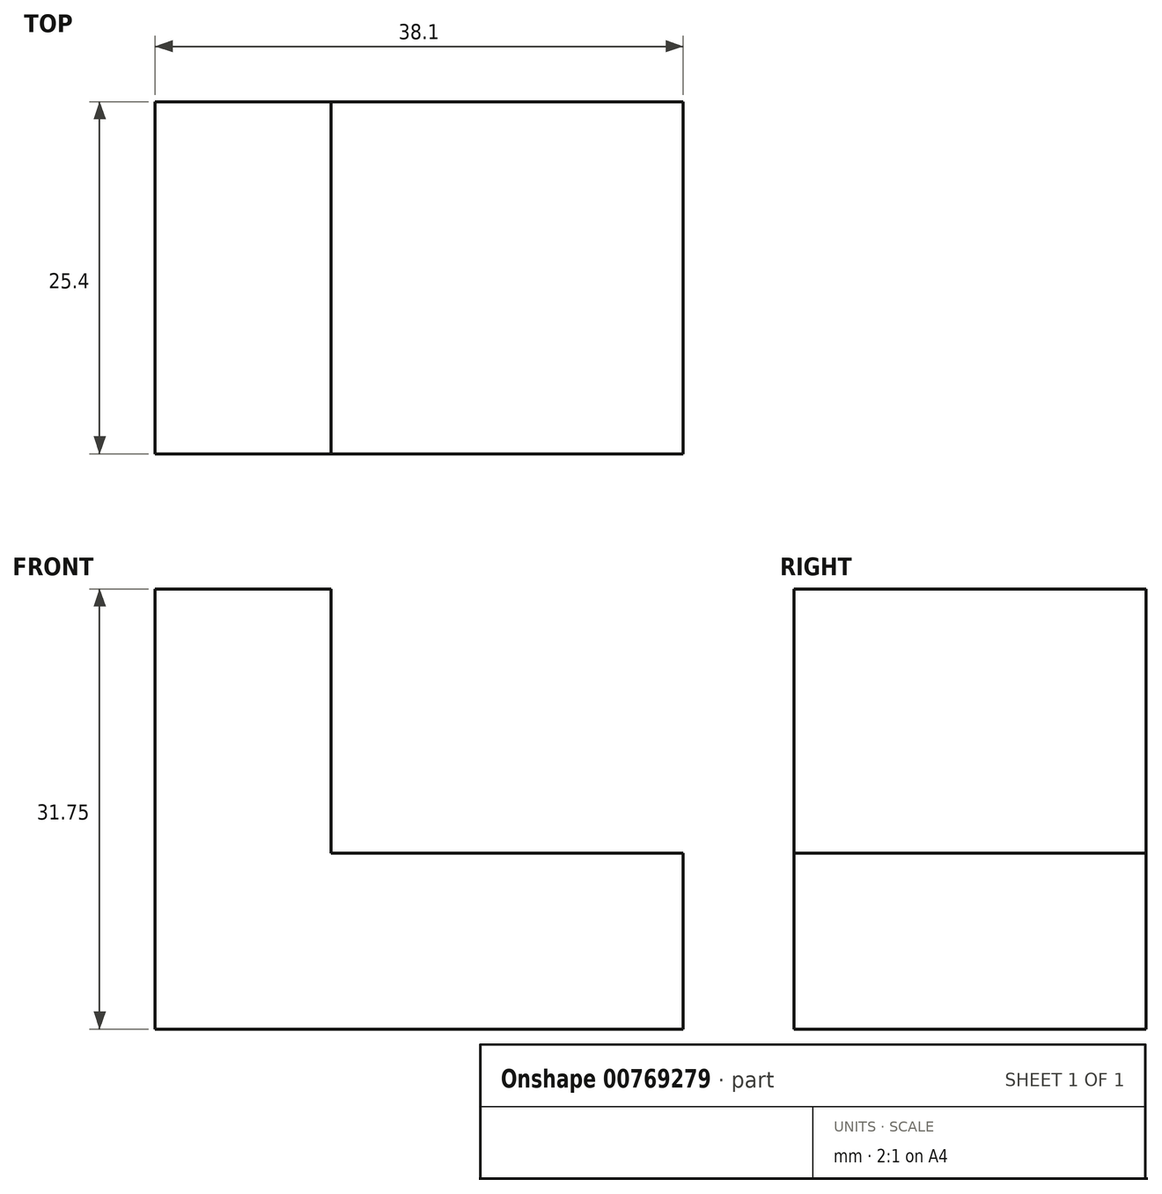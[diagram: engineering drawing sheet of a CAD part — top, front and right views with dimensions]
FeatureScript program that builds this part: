
annotation { "Feature Type Name" : "Feature", "Feature Type Description" : "" }
export const myFeature = defineFeature(function(context is Context, id is Id, definition is map)
    precondition{}
    {
        {
            var Q0;
            Q0=qCreatedBy(makeId("Front.planeOp"),FACE);
            var sketch = newSketch(context, id + "F0", { "sketchPlane" : qUnion([Q0])});
            skLineSegment(sketch, "E0", {"start": v(0, 0) * mm, "end": v(0, 31.75) * mm});
            skLineSegment(sketch, "E1", {"start": v(0, 31.75) * mm, "end": v(0, 0) * mm});
            skLineSegment(sketch, "E2", {"start": v(0, 31.75) * mm, "end": v(12.7, 31.75) * mm});
            skLineSegment(sketch, "E3", {"start": v(12.7, 31.75) * mm, "end": v(12.7, 12.7) * mm});
            skLineSegment(sketch, "E4", {"start": v(12.7, 12.7) * mm, "end": v(38.1, 12.7) * mm});
            skLineSegment(sketch, "E5", {"start": v(38.1, 12.7) * mm, "end": v(38.1, 0) * mm});
            skLineSegment(sketch, "E6", {"start": v(38.1, 0) * mm, "end": v(0, 0) * mm});
            skLineSegment(sketch, "E7", {"start": v(38.1, 0) * mm, "end": v(30.55, 5.43) * mm});
            skSolve(sketch);
        }
        {
            var Q0;
            Q0 = qSketchRegion(id + "F0", true);
            extrude(context, id + "F1", {"entities" : qUnion([Q0]), "depth" : 25.4 * mm, "offsetDistance" : 25.4 * mm});
        }
    });
